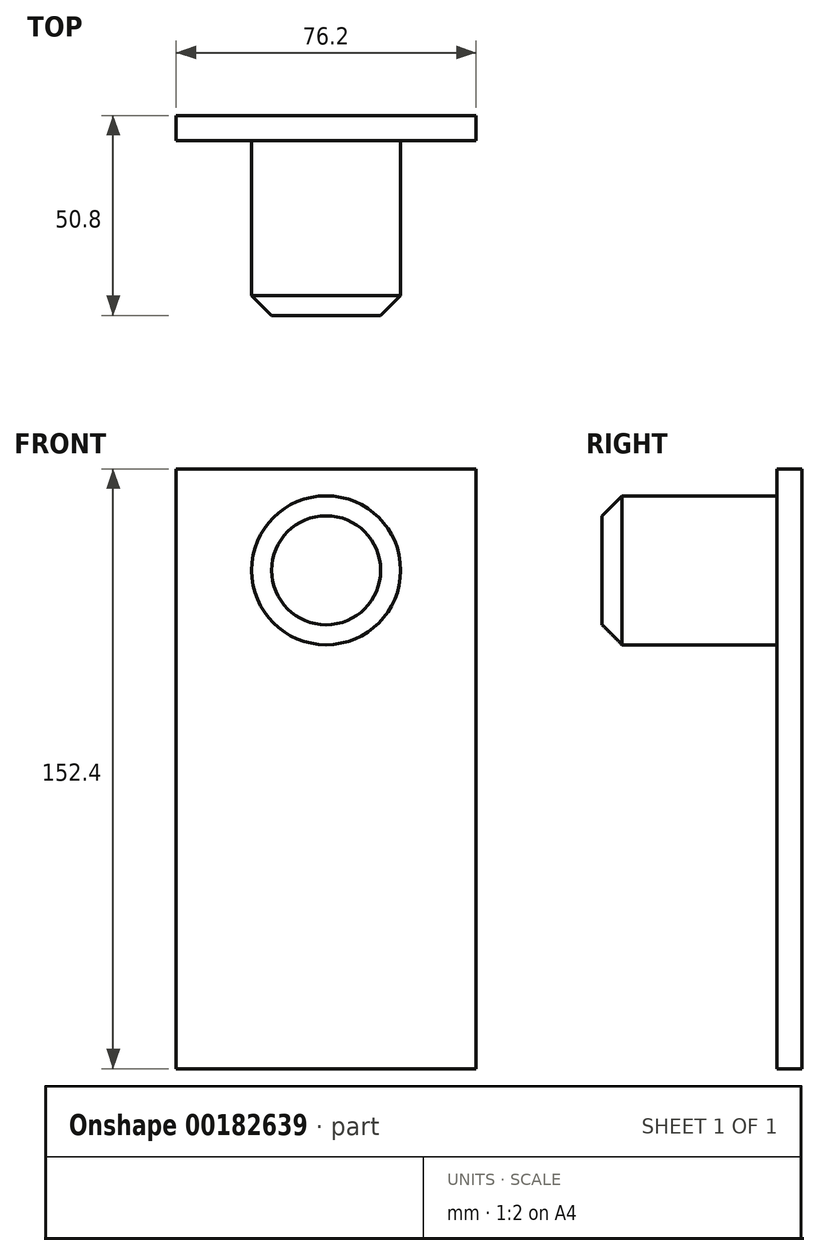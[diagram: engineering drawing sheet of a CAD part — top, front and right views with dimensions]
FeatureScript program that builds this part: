
annotation { "Feature Type Name" : "Feature", "Feature Type Description" : "" }
export const myFeature = defineFeature(function(context is Context, id is Id, definition is map)
    precondition{}
    {
        {
            var Q0;
            Q0=qCreatedBy(makeId("Front.planeOp"),FACE);
            var sketch = newSketch(context, id + "F0", { "sketchPlane" : qUnion([Q0])});
            skLineSegment(sketch, "E0.bottom", {"start": v(-38.1, 76.2) * mm, "end": v(38.1, 76.2) * mm});
            skLineSegment(sketch, "E0.top", {"start": v(-38.1, -76.2) * mm, "end": v(38.1, -76.2) * mm});
            skLineSegment(sketch, "E0.left", {"start": v(-38.1, 76.2) * mm, "end": v(-38.1, -76.2) * mm});
            skLineSegment(sketch, "E0.right", {"start": v(38.1, 76.2) * mm, "end": v(38.1, -76.2) * mm});
            skPoint(sketch, "E0.middle", {"position": v(0, 0) * mm});
            skSolve(sketch);
        }
        {
            var Q0;
            Q0=makeQuery(id+"F0.imprint","IMPRINT",FACE,{"disambiguationData":[TD([[makeQuery(id+"F0.imprint","IMPRINT",EDGE,{"derivedFrom":sQuery(id+"F0.wireOp",EDGE,"E0.bottom")}),-1.0]])]});
            var sketch = newSketch(context, id + "F1", { "sketchPlane" : qUnion([Q0])});
            skCircle(sketch, "E1", {"center": v(0, 50.43) * mm, "radius": 18.92 * mm});
            skSolve(sketch);
        }
        {
            var Q0;
            Q0=makeQuery(id+"F1.imprint","IMPRINT",FACE,{"disambiguationData":[TD([[makeQuery(id+"F1.imprint","IMPRINT",EDGE,{"derivedFrom":sQuery(id+"F1.wireOp",EDGE,"E1")}),1.0]])]});
            extrude(context, id + "F2", {"entities" : qUnion([Q0]), "depth" : 50.8 * mm});
        }
        {
            var Q0;
            Q0=makeQuery(id+"F0.imprint","IMPRINT",FACE,{"disambiguationData":[TD([[makeQuery(id+"F0.imprint","IMPRINT",EDGE,{"derivedFrom":sQuery(id+"F0.wireOp",EDGE,"E0.bottom")}),-1.0]])]});
            extrude(context, id + "F3", {"entities" : qUnion([Q0]), "operationType" : NewBodyOperationType.ADD, "depth" : 6.35 * mm});
        }
        {
            var Q0;
            Q0=makeQuery(id+"F2.opExtrude","CAP_EDGE",EDGE,{"disambiguationData":[OSD([sQuery(id+"F1.wireOp",EDGE,"E1")])],"isStart":false});
            chamfer(context, id + "F4", {"entities" : qUnion([Q0]), "width" : 5.08 * mm, "tangentPropagation" : true});
        }
    });
